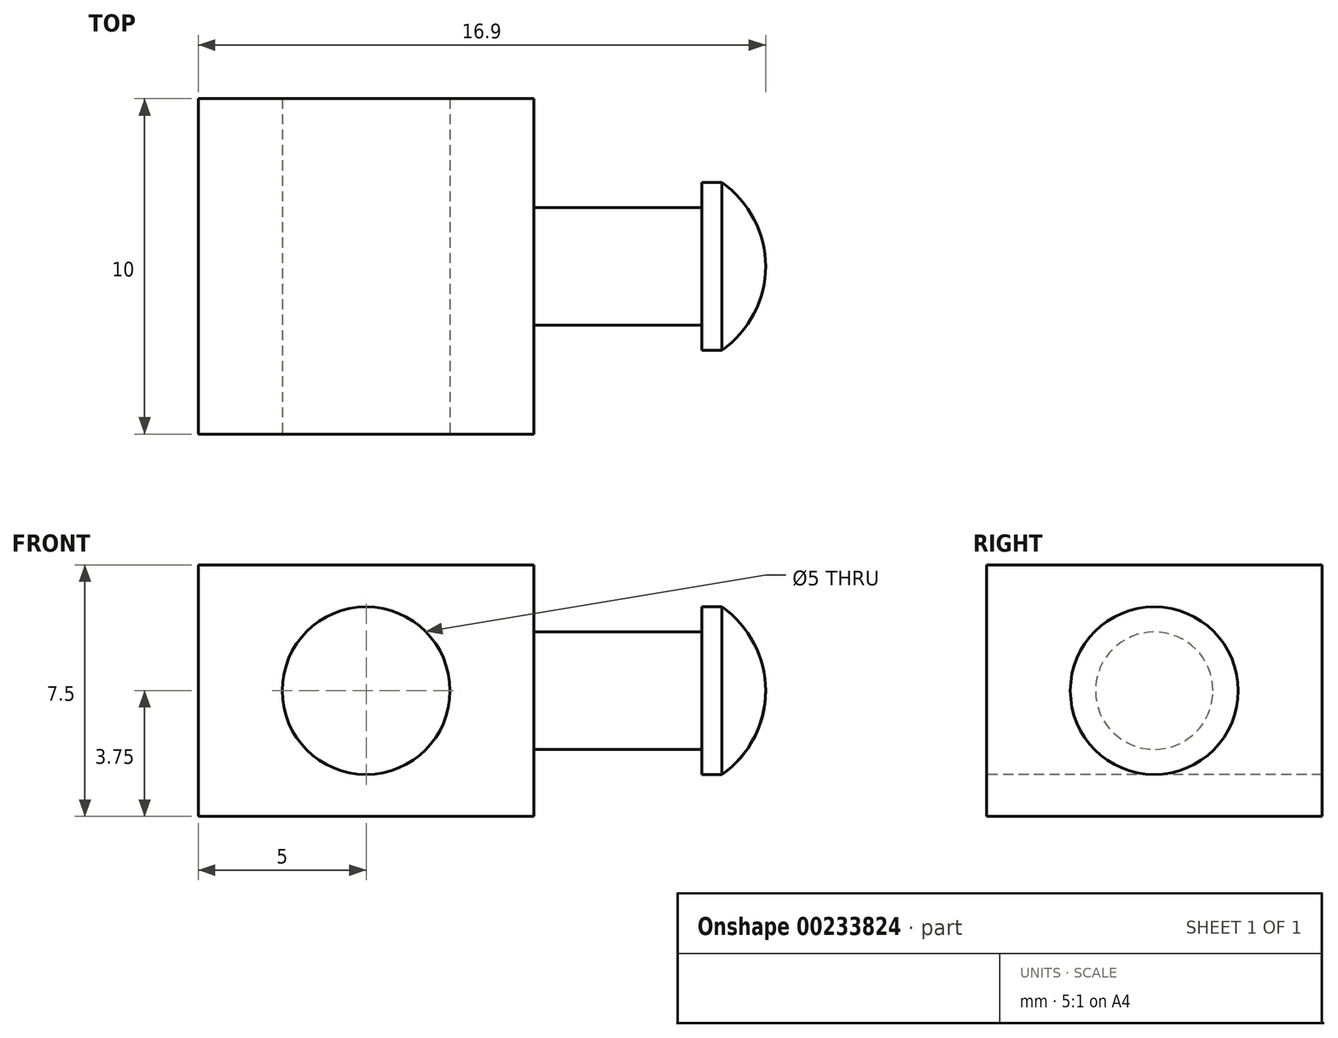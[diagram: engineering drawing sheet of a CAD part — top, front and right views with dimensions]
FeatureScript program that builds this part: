
annotation { "Feature Type Name" : "Feature", "Feature Type Description" : "" }
export const myFeature = defineFeature(function(context is Context, id is Id, definition is map)
    precondition{}
    {
        {
            var Q0;
            Q0=qCreatedBy(makeId("Front.planeOp"),FACE);
            var sketch = newSketch(context, id + "F0", { "sketchPlane" : qUnion([Q0])});
            skLineSegment(sketch, "E0.bottom", {"start": v(5, 3.75) * mm, "end": v(-5, 3.75) * mm});
            skLineSegment(sketch, "E0.top", {"start": v(5, -3.75) * mm, "end": v(-5, -3.75) * mm});
            skLineSegment(sketch, "E0.left", {"start": v(5, 3.75) * mm, "end": v(5, -3.75) * mm});
            skLineSegment(sketch, "E0.right", {"start": v(-5, 3.75) * mm, "end": v(-5, -3.75) * mm});
            skPoint(sketch, "E0.middle", {"position": v(0, 0) * mm});
            skLineSegment(sketch, "E1", {"start": v(5, 0) * mm, "end": v(10, 0) * mm});
            skPoint(sketch, "E1.endSnap0", {"position": v(5, 0) * mm});
            skLineSegment(sketch, "E2", {"start": v(10, 0) * mm, "end": v(10, 1.75) * mm});
            skLineSegment(sketch, "E3", {"start": v(10, 1.75) * mm, "end": v(5, 1.75) * mm});
            skLineSegment(sketch, "E4", {"start": v(10, 1.75) * mm, "end": v(10, 2.5) * mm});
            skLineSegment(sketch, "E5", {"start": v(10, 2.5) * mm, "end": v(10.6, 2.5) * mm});
            skLineSegment(sketch, "E6", {"start": v(10.6, 2.5) * mm, "end": v(10.6, 0) * mm});
            skLineSegment(sketch, "E7", {"start": v(10, 0) * mm, "end": v(14.33, 0) * mm});
            skLineSegment(sketch, "E8.MirrorCS", {"start": v(10.6, -2.5) * mm, "end": v(10.6, 0) * mm});
            skLineSegment(sketch, "E9.MirrorCS", {"start": v(10, 0) * mm, "end": v(10, -1.75) * mm});
            skLineSegment(sketch, "E10.MirrorCS", {"start": v(10, -1.75) * mm, "end": v(10, -2.5) * mm});
            skLineSegment(sketch, "E11.MirrorCS", {"start": v(10, -2.5) * mm, "end": v(10.6, -2.5) * mm});
            skArc(sketch, "E12", {"start": v(11.9, 0) * mm, "mid": v(11.56, 1.4) * mm, "end": v(10.6, 2.5) * mm});
            skSolve(sketch);
        }
        {
            var Q0;
            {var subQ3=sQuery(id+"F0.wireOp",EDGE,"E0.bottom");Q0=makeQuery(id+"F0.imprint","IMPRINT",FACE,{"disambiguationData":[TD([[makeQuery(id+"F0.imprint","IMPRINT",EDGE,{"derivedFrom":subQ3}),1.0]])]});}
            extrude(context, id + "F1", {"entities" : qUnion([Q0]), "endBound" : BoundingType.SYMMETRIC, "depth" : 10 * mm});
        }
        {
            var Q0;
            {var subQ0=sQuery(id+"F0.wireOp",EDGE,"E1");Q0=makeQuery(id+"F0.imprint","IMPRINT",FACE,{"disambiguationData":[TD([[makeQuery(id+"F0.imprint","IMPRINT",EDGE,{"derivedFrom":subQ0}),1.0]])]});}
            var Q1;
            Q1=sQuery(id+"F0.wireOp",EDGE,"E1");
            revolve(context, id + "F2", {"operationType" : NewBodyOperationType.ADD, "entities" : qUnion([Q0]), "axis" : qUnion([Q1]), "revolveType" : RevolveType.FULL});
        }
        {
            var Q0;
            {var subQ1=sQuery(id+"F0.wireOp",EDGE,"E2");Q0=makeQuery(id+"F0.imprint","IMPRINT",FACE,{"disambiguationData":[TD([[makeQuery(id+"F0.imprint","IMPRINT",EDGE,{"derivedFrom":subQ1}),-1.0]])]});}
            var Q1;
            {var subQ0=sQuery(id+"F0.wireOp",EDGE,"E7");var subQ3=sQuery(id+"F0.wireOp",EDGE,"nhdbmaDL-lB7M-k7X0-U7D3-Sq6NFg3OUXmD");var subQ5=makeQuery(id+"F0.imprint","INTERSECT",VERTEX,{"derivedFrom":[subQ0,subQ3]});Q1=makeQuery(id+"F0.imprint","IMPRINT",FACE,{"disambiguationData":[TD([[makeQuery(id+"F0.imprint","IMPRINT",EDGE,{"disambiguationData":[TD([[subQ5,-1.0]])],"derivedFrom":subQ3}),1.0]])]});}
            var Q2;
            Q2=sQuery(id+"F0.wireOp",EDGE,"E7");
            revolve(context, id + "F3", {"operationType" : NewBodyOperationType.ADD, "entities" : qUnion([Q0, Q1]), "axis" : qUnion([Q2]), "revolveType" : RevolveType.FULL});
        }
        {
            var Q0;
            {var subQ0=sQuery(id+"F0.wireOp",EDGE,"E6");Q0=makeQuery(id+"F0.imprint","IMPRINT",FACE,{"disambiguationData":[TD([[makeQuery(id+"F0.imprint","IMPRINT",EDGE,{"derivedFrom":subQ0}),1.0]])]});}
            var Q1;
            Q1=sQuery(id+"F0.wireOp",EDGE,"E7");
            revolve(context, id + "F4", {"operationType" : NewBodyOperationType.ADD, "entities" : qUnion([Q0]), "axis" : qUnion([Q1]), "revolveType" : RevolveType.FULL});
        }
        {
            var Q0;
            Q0=makeQuery(id+"F1.opExtrude","CAP_FACE",FACE,{"disambiguationData":[OSD([sQuery(id+"F0.wireOp",EDGE,"E0.bottom"),sQuery(id+"F0.wireOp",EDGE,"E0.top"),sQuery(id+"F0.wireOp",EDGE,"E0.left"),sQuery(id+"F0.wireOp",EDGE,"E0.right")])],"isStart":false});
            var sketch = newSketch(context, id + "F5", { "sketchPlane" : qUnion([Q0])});
            skCircle(sketch, "E13", {"center": v(0, 0) * mm, "radius": 2.5 * mm});
            skSolve(sketch);
        }
        {
            var Q0;
            Q0=makeQuery(id+"F5.imprint","IMPRINT",FACE,{"disambiguationData":[TD([[makeQuery(id+"F5.imprint","IMPRINT",EDGE,{"derivedFrom":sQuery(id+"F5.wireOp",EDGE,"E13")}),1.0]])]});
            extrude(context, id + "F6", {"entities" : qUnion([Q0]), "operationType" : NewBodyOperationType.REMOVE, "oppositeDirection" : true, "depth" : 25 * mm});
        }
    });
